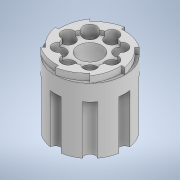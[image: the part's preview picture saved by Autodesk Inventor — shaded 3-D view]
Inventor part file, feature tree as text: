
AUTODESK INVENTOR PART (.ipt)
format: ipt  version: 2021 (Build 250183000, 183)  size: 310,272 bytes
history: native  units: in
note: dims shown in document units (in); Inventor stores cm internally (conversion verified against a paired STEP export)
features: extrude x9, sketch x9, pattern_circular x2, direct_edit x1, other x1
ambient origin geometry x8: Origin, YZ Plane, XZ Plane, XY Plane, X Axis, Y Axis, Z Axis, Center Point
bodies: Solid1 (feature_tree)
feature tree (22):
  extrude  "Extrusion1"  Depth=33.0in TaperAngle=0.0deg
  extrude  "Extrusion2"  Depth=4.0in
  extrude  "Extrusion3"  Depth=3.1496in TaperAngle=360.0deg
  extrude  "Extrusion4"  Depth=14.3in
  extrude  "Extrusion5"  Depth=1.0in TaperAngle=0.0deg
  extrude  "Extrusion6"  Depth=2.0in TaperAngle=0.0deg
  extrude  "Extrusion8"  Depth=20.0in TaperAngle=0.0deg
  pattern_circular  "Circular Pattern2"  Count=8 Angle=360.0deg
  extrude  "Extrusion9"  Depth=0.3937in
  extrude  "Extrusion10"  Depth=0.3937in
  pattern_circular  "Circular Pattern3"  [2 undecoded]
  direct_edit  "Direct Edit1"
  sketch  "Sketch1"  dims[d0=32.0in d1=33.0in d2=0.0in]
  sketch  "Sketch2"  dims[d3=8.0in d4=4.0in]
  sketch  "Sketch4"  dims[d5=10.0in d6=3.1496in d8=360.0deg]
  sketch  "Sketch5"  dims[d10=0.0in d11=0.0in d13=14.3in]
  sketch  "Sketch6"  dims[d14=10.0in d15=1.0in d16=0.0in]
  sketch  "Sketch8"  dims[d17=20.5in d18=2.0in d19=0.0in]
  sketch  "Sketch10"  dims[d20=11.0in d21=20.0in d22=0.0in]
  sketch  "Sketch11"  dims[d23=6.0in d24=3.1496in d26=360.0deg]
  sketch  "Sketch12"  dims[d28=23.0in d29=0.0in d56=1.715in d57=3.192in d58=36.0in d59=10.253in d60=1.0607in d61=3.0in d62=0.0in d63=3.1496in d64=360.0deg d66=2.0in d67=5.5in d68=0.0in d69=15.5in d70=0.0in d71=5.0in d72=11.314in d73=11.314in d75=16.0in d76=22.5in d77=0.0in d78=3.1496in d79=360.0deg d83=0.0155in d84=0.3937in d85=0.3937in]
  other  "Scale1"
note: 2 required parameter values undecoded (feature->parameter linkage not recoverable at this tier; creation-order binding heuristic only, values carry confidence <= 0.55)
